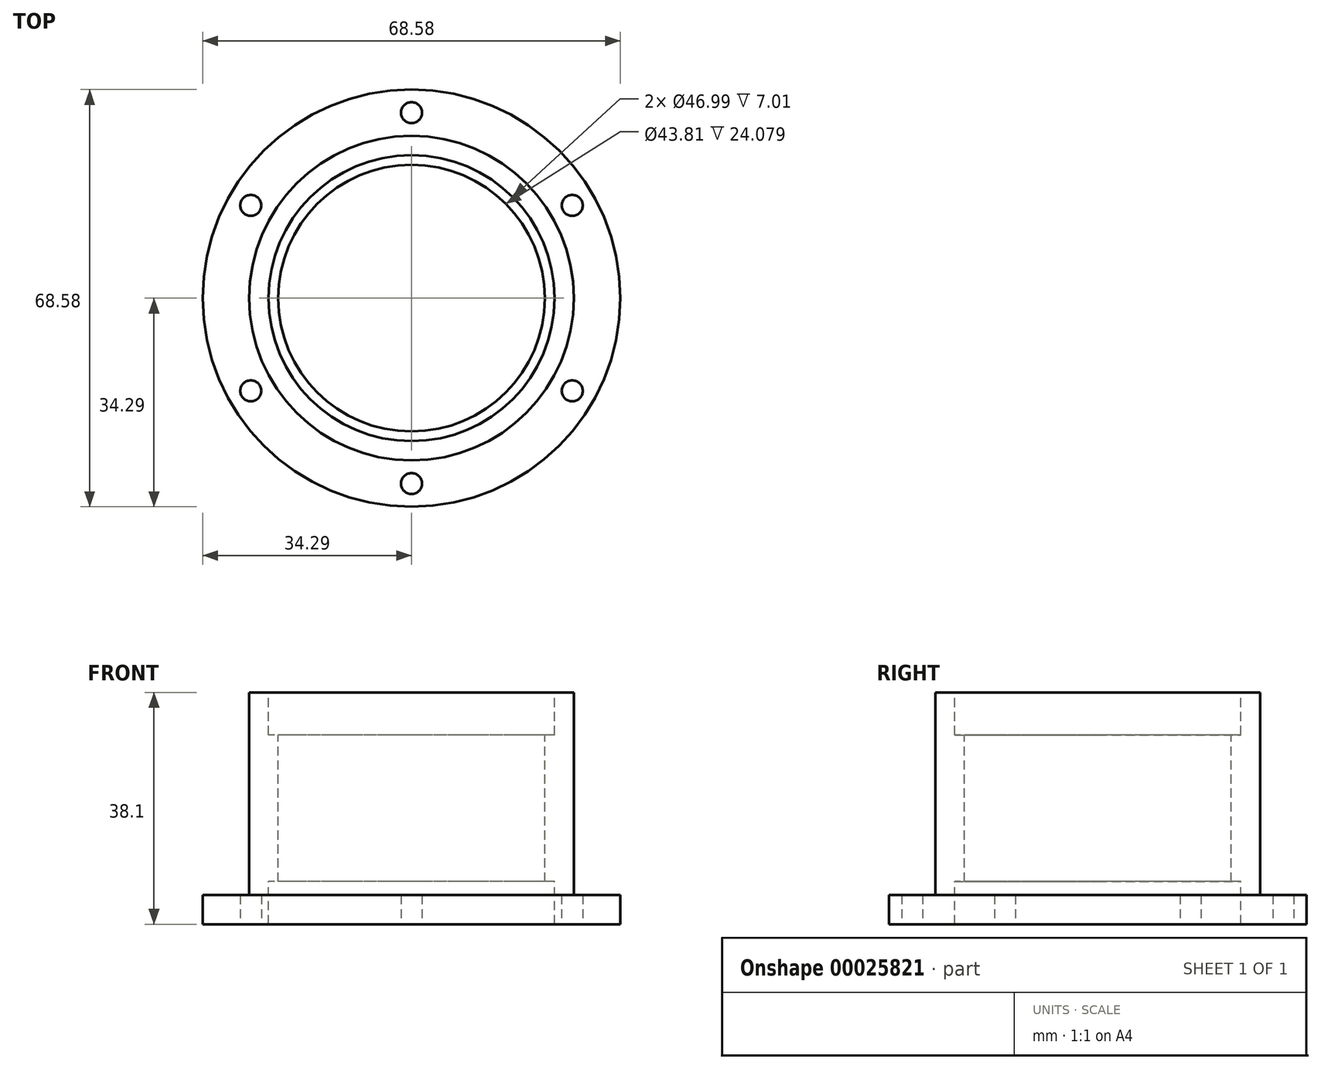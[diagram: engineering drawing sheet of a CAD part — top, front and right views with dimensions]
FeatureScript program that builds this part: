
annotation { "Feature Type Name" : "Feature", "Feature Type Description" : "" }
export const myFeature = defineFeature(function(context is Context, id is Id, definition is map)
    precondition{}
    {
        {
            var Q0;
            Q0=qCreatedBy(makeId("Front.planeOp"),FACE);
            var sketch = newSketch(context, id + "F0", { "sketchPlane" : qUnion([Q0])});
            skLineSegment(sketch, "E0", {"start": v(0, 38.23) * mm, "end": v(0, 0) * mm, "construction": true});
            skLineSegment(sketch, "E1", {"start": v(0, 0) * mm, "end": v(-23.5, 0) * mm, "construction": true});
            skLineSegment(sketch, "E2.bottom", {"start": v(-23.5, 0) * mm, "end": v(-34.3, 0) * mm});
            skLineSegment(sketch, "E2.top", {"start": v(-23.5, 38.1) * mm, "end": v(-26.67, 38.1) * mm});
            skLineSegment(sketch, "E2.left", {"start": v(-23.5, 0) * mm, "end": v(-23.5, 7.01) * mm});
            skLineSegment(sketch, "E2.right", {"start": v(-34.3, 0) * mm, "end": v(-34.3, 4.78) * mm});
            skLineSegment(sketch, "E3.bottom", {"start": v(-23.5, 31.09) * mm, "end": v(-21.9, 31.09) * mm});
            skLineSegment(sketch, "E3.top", {"start": v(-23.5, 7.01) * mm, "end": v(-21.9, 7.01) * mm});
            skLineSegment(sketch, "E3.right", {"start": v(-21.9, 31.09) * mm, "end": v(-21.9, 7.01) * mm});
            skLineSegment(sketch, "E4.bottom", {"start": v(-26.67, 4.78) * mm, "end": v(-34.3, 4.78) * mm});
            skLineSegment(sketch, "E4.left", {"start": v(-26.67, 4.78) * mm, "end": v(-26.67, 38.1) * mm});
            skLineSegment(sketch, "E5.trimOffspring", {"start": v(-23.5, 31.09) * mm, "end": v(-23.5, 38.1) * mm});
            skSolve(sketch);
        }
        {
            var Q0;
            Q0=makeQuery(id+"F0.imprint","IMPRINT",FACE,{"disambiguationData":[TD([[makeQuery(id+"F0.imprint","IMPRINT",EDGE,{"derivedFrom":sQuery(id+"F0.wireOp",EDGE,"E2.bottom")}),-1.0]])]});
            var Q1;
            Q1=sQuery(id+"F0.wireOp",EDGE,"E0");
            revolve(context, id + "F1", {"entities" : qUnion([Q0]), "axis" : qUnion([Q1]), "revolveType" : RevolveType.FULL});
        }
        {
            var Q0;
            Q0=makeQuery(id+"F1.opRevolve","SWEPT_FACE",FACE,{"disambiguationData":[OSD([sQuery(id+"F0.wireOp",EDGE,"E2.bottom")])]});
            var sketch = newSketch(context, id + "F2", { "sketchPlane" : qUnion([Q0])});
            skLineSegment(sketch, "E6", {"start": v(0, 0) * mm, "end": v(0, 30.48) * mm});
            skLineSegment(sketch, "E7.1.0", {"start": v(0, 0) * mm, "end": v(-26.4, 15.24) * mm});
            skLineSegment(sketch, "E7.2.0", {"start": v(0, 0) * mm, "end": v(-26.4, -15.24) * mm});
            skLineSegment(sketch, "E7.3.0", {"start": v(0, 0) * mm, "end": v(0, -30.48) * mm});
            skLineSegment(sketch, "E7.4.0", {"start": v(0, 0) * mm, "end": v(26.4, -15.24) * mm});
            skLineSegment(sketch, "E7.5.0", {"start": v(0, 0) * mm, "end": v(26.4, 15.24) * mm});
            skPoint(sketch, "E7.center", {"position": v(0, 0) * mm});
            skSolve(sketch);
        }
        {
            var Q0;
            Q0=sQuery(id+"F2.wireOp",VERTEX,"E7.1.0.end");
            var Q1;
            Q1=sQuery(id+"F2.wireOp",VERTEX,"E6.end");
            var Q2;
            Q2=sQuery(id+"F2.wireOp",VERTEX,"E7.5.0.end");
            var Q3;
            Q3=sQuery(id+"F2.wireOp",VERTEX,"E7.4.0.end");
            var Q4;
            Q4=sQuery(id+"F2.wireOp",VERTEX,"E7.3.0.end");
            var Q5;
            Q5=sQuery(id+"F2.wireOp",VERTEX,"E7.2.0.end");
            var Q6;
            Q6=makeQuery(id+"F1.opRevolve","SWEPT_BODY",BODY,{"disambiguationData":[OSD([sQuery(id+"F0.wireOp",EDGE,"E2.bottom"),sQuery(id+"F0.wireOp",EDGE,"E2.top"),sQuery(id+"F0.wireOp",EDGE,"E2.left"),sQuery(id+"F0.wireOp",EDGE,"E2.right"),sQuery(id+"F0.wireOp",EDGE,"E3.bottom"),sQuery(id+"F0.wireOp",EDGE,"E3.top"),sQuery(id+"F0.wireOp",EDGE,"E3.right"),sQuery(id+"F0.wireOp",EDGE,"E4.bottom"),sQuery(id+"F0.wireOp",EDGE,"E4.left"),sQuery(id+"F0.wireOp",EDGE,"E5.trimOffspring")])]});
            hole(context, id + "F3", {"style" : HoleStyle.SIMPLE, "holeDiameter" : 3.45 * mm, "endStyle" : HoleEndStyle.THROUGH, "locations" : qUnion([Q0, Q1, Q2, Q3, Q4, Q5]), "scope" : qUnion([Q6])});
        }
    });
